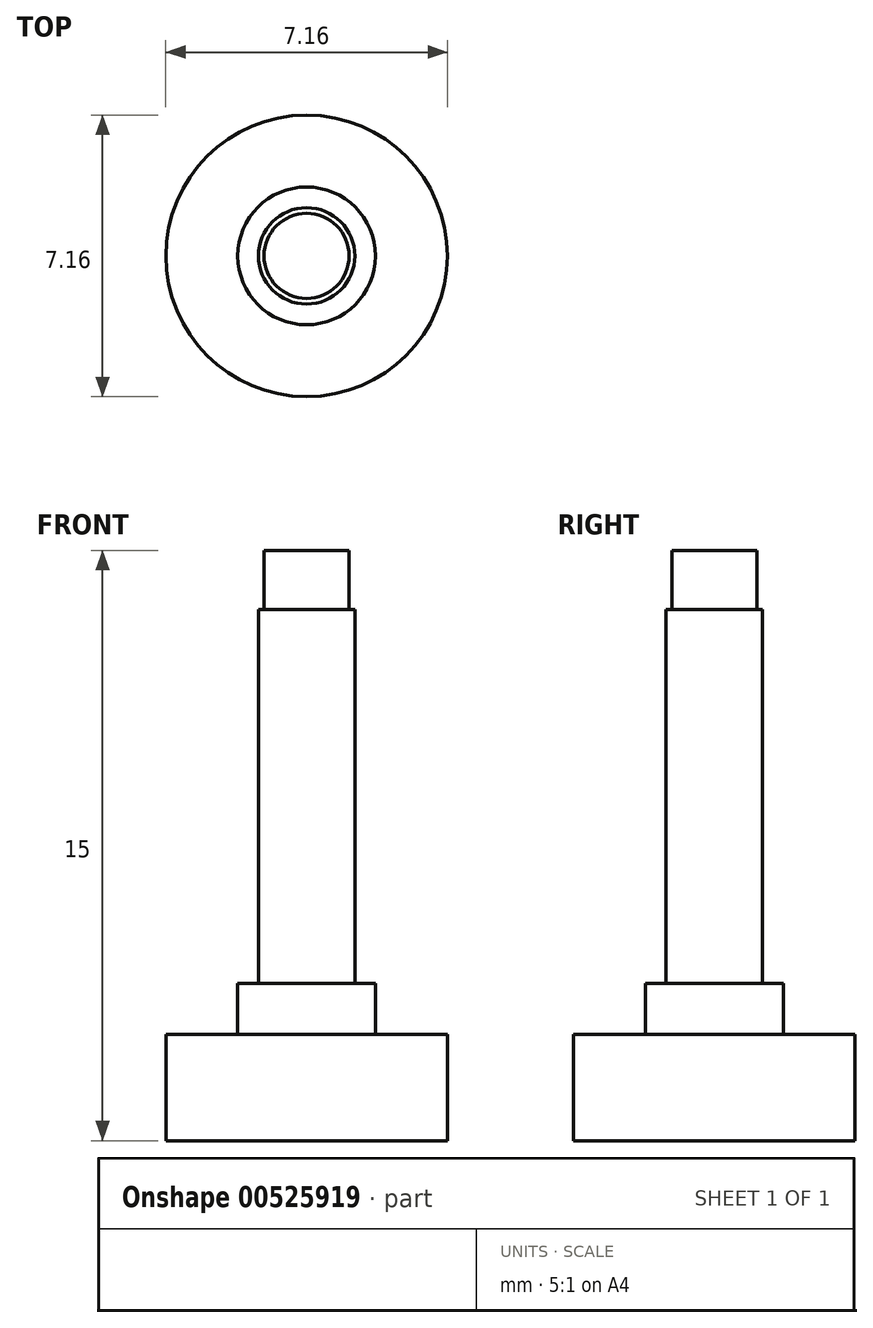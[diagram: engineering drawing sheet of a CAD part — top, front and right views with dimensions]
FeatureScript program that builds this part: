
annotation { "Feature Type Name" : "Feature", "Feature Type Description" : "" }
export const myFeature = defineFeature(function(context is Context, id is Id, definition is map)
    precondition{}
    {
        {
            var Q0;
            Q0=qCreatedBy(makeId("Top.planeOp"),FACE);
            var sketch = newSketch(context, id + "F0", { "sketchPlane" : qUnion([Q0])});
            skCircle(sketch, "E0", {"center": v(0, 0) * mm, "radius": 3.58 * mm});
            skCircle(sketch, "E1", {"center": v(0, 0) * mm, "radius": 1.75 * mm});
            skCircle(sketch, "E2", {"center": v(0, 0) * mm, "radius": 1.23 * mm});
            skCircle(sketch, "E3", {"center": v(0, 0) * mm, "radius": 1.08 * mm});
            skSolve(sketch);
        }
        {
            var Q0;
            Q0=makeQuery(id+"F0.imprint","IMPRINT",FACE,{"disambiguationData":[TD([[makeQuery(id+"F0.imprint","IMPRINT",EDGE,{"derivedFrom":sQuery(id+"F0.wireOp",EDGE,"E3")}),1.0]])]});
            extrude(context, id + "F1", {"entities" : qUnion([Q0]), "depth" : 15 * mm, "offsetDistance" : 25 * mm});
        }
        {
            var Q0;
            Q0=makeQuery(id+"F0.imprint","IMPRINT",FACE,{"disambiguationData":[TD([[makeQuery(id+"F0.imprint","IMPRINT",EDGE,{"derivedFrom":sQuery(id+"F0.wireOp",EDGE,"E2")}),1.0]])]});
            extrude(context, id + "F2", {"entities" : qUnion([Q0]), "operationType" : NewBodyOperationType.ADD, "depth" : 13.5 * mm, "offsetDistance" : 25 * mm});
        }
        {
            var Q0;
            Q0=makeQuery(id+"F0.imprint","IMPRINT",FACE,{"disambiguationData":[TD([[makeQuery(id+"F0.imprint","IMPRINT",EDGE,{"derivedFrom":sQuery(id+"F0.wireOp",EDGE,"E1")}),1.0]])]});
            extrude(context, id + "F3", {"entities" : qUnion([Q0]), "operationType" : NewBodyOperationType.ADD, "depth" : 4 * mm, "offsetDistance" : 25 * mm});
        }
        {
            var Q0;
            Q0=makeQuery(id+"F0.imprint","IMPRINT",FACE,{"disambiguationData":[TD([[makeQuery(id+"F0.imprint","IMPRINT",EDGE,{"derivedFrom":sQuery(id+"F0.wireOp",EDGE,"E0")}),1.0]])]});
            extrude(context, id + "F4", {"entities" : qUnion([Q0]), "operationType" : NewBodyOperationType.ADD, "depth" : 2.7 * mm, "offsetDistance" : 25 * mm});
        }
    });
